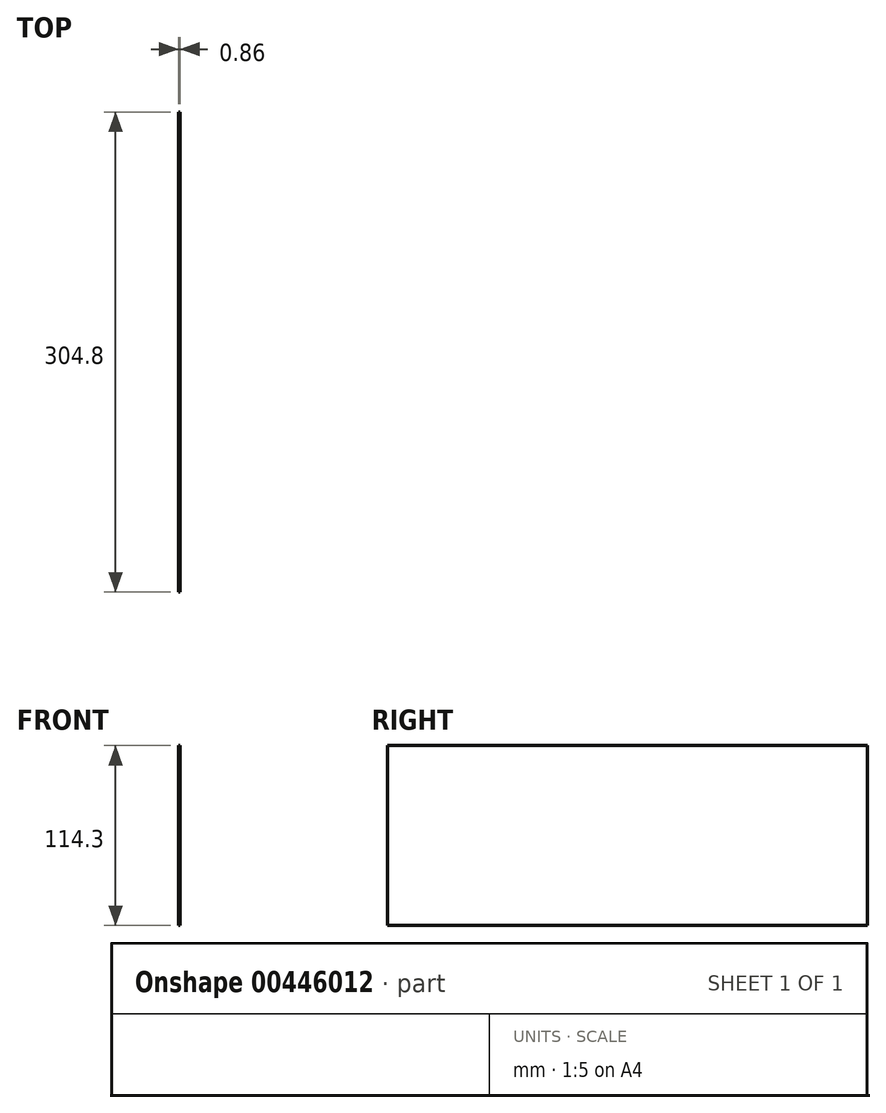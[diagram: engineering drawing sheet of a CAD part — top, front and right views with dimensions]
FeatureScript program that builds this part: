
annotation { "Feature Type Name" : "Feature", "Feature Type Description" : "" }
export const myFeature = defineFeature(function(context is Context, id is Id, definition is map)
    precondition{}
    {
        {
            var Q0;
            Q0=qCreatedBy(makeId("Front.planeOp"),FACE);
            var sketch = newSketch(context, id + "F0", { "sketchPlane" : qUnion([Q0])});
            skLineSegment(sketch, "E0.bottom", {"start": v(-0.43, 57.15) * mm, "end": v(0.43, 57.15) * mm});
            skLineSegment(sketch, "E0.top", {"start": v(-0.43, -57.15) * mm, "end": v(0.43, -57.15) * mm});
            skLineSegment(sketch, "E0.left", {"start": v(-0.43, 57.15) * mm, "end": v(-0.43, -57.15) * mm});
            skLineSegment(sketch, "E0.right", {"start": v(0.43, 57.15) * mm, "end": v(0.43, -57.15) * mm});
            skPoint(sketch, "E0.middle", {"position": v(0, 0) * mm});
            skSolve(sketch);
        }
        {
            var Q0;
            Q0 = qSketchRegion(id + "F0", true);
            extrude(context, id + "F1", {"entities" : qUnion([Q0]), "oppositeDirection" : true, "depth" : 304.8 * mm, "offsetDistance" : 25.4 * mm});
        }
    });
